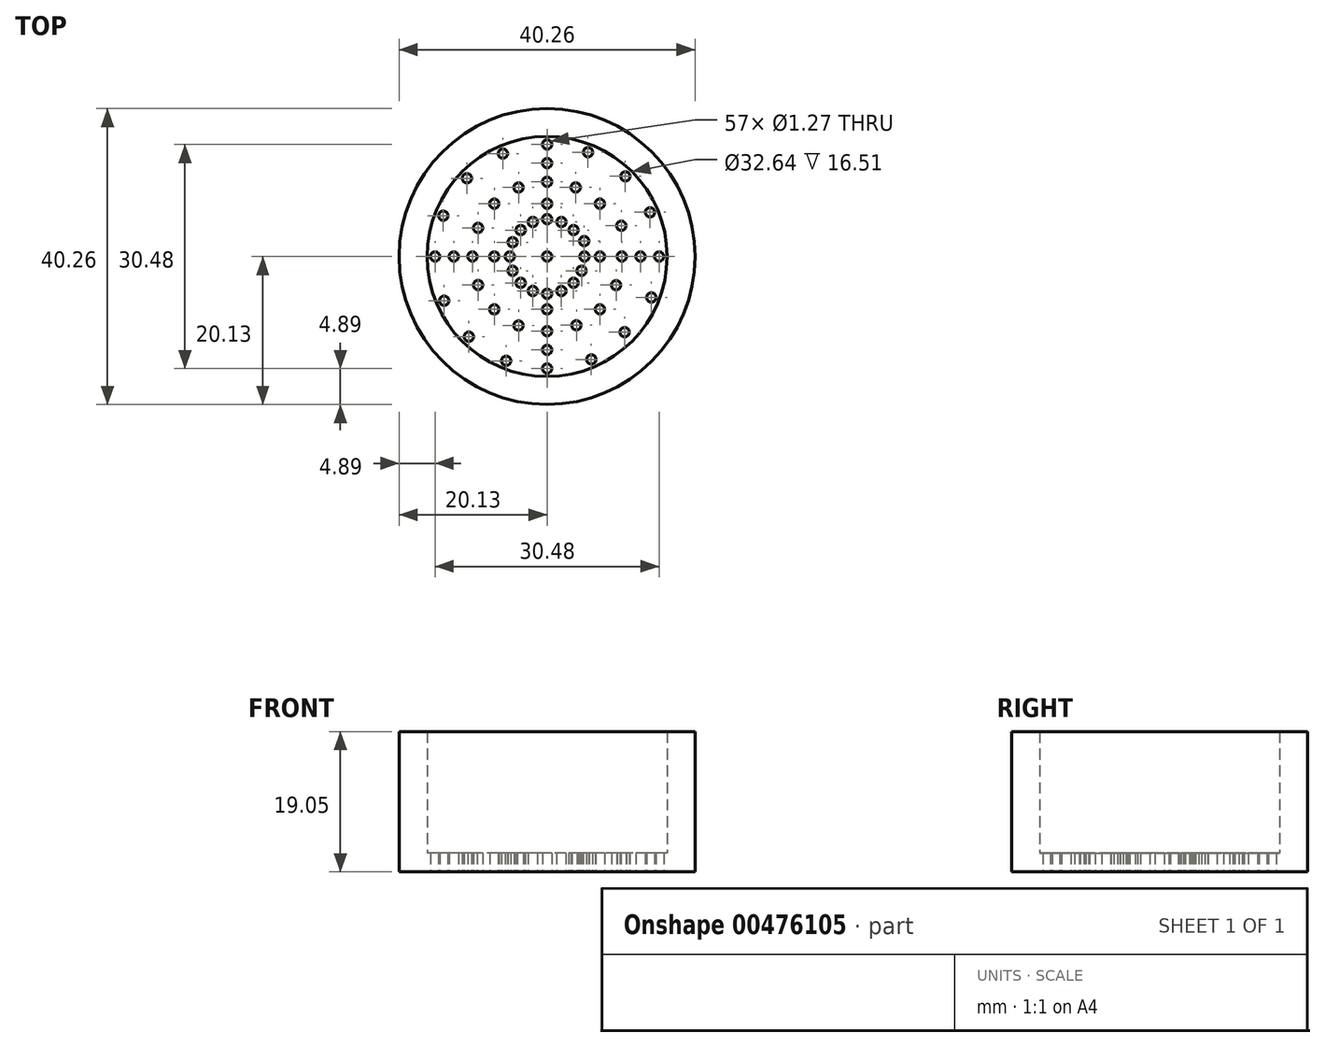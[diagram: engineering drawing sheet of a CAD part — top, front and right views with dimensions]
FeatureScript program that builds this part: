
annotation { "Feature Type Name" : "Feature", "Feature Type Description" : "" }
export const myFeature = defineFeature(function(context is Context, id is Id, definition is map)
    precondition{}
    {
        {
            var Q0;
            Q0=qCreatedBy(makeId("Top.planeOp"),FACE);
            var sketch = newSketch(context, id + "F0", { "sketchPlane" : qUnion([Q0])});
            skCircle(sketch, "E0", {"center": v(0, 0) * mm, "radius": 16.32 * mm});
            skCircle(sketch, "E1", {"center": v(0, 0) * mm, "radius": 20.13 * mm});
            skCircle(sketch, "E2", {"center": v(0, 10.16) * mm, "radius": 0.64 * mm});
            skCircle(sketch, "E3", {"center": v(3.89, 9.39) * mm, "radius": 0.64 * mm});
            skCircle(sketch, "E4", {"center": v(1.94, 4.7) * mm, "radius": 0.64 * mm});
            skCircle(sketch, "E5", {"center": v(3.6, 3.6) * mm, "radius": 0.64 * mm});
            skCircle(sketch, "E6", {"center": v(7.18, 7.18) * mm, "radius": 0.64 * mm});
            skCircle(sketch, "E7", {"center": v(10.1, 4.18) * mm, "radius": 0.64 * mm});
            skCircle(sketch, "E8", {"center": v(10.16, 0) * mm, "radius": 0.64 * mm});
            skCircle(sketch, "E9", {"center": v(-3.89, 9.39) * mm, "radius": 0.64 * mm});
            skCircle(sketch, "E10", {"center": v(-1.94, 4.7) * mm, "radius": 0.64 * mm});
            skCircle(sketch, "E11", {"center": v(5.08, 0) * mm, "radius": 0.64 * mm});
            skCircle(sketch, "E12", {"center": v(9.39, -3.89) * mm, "radius": 0.64 * mm});
            skCircle(sketch, "E13", {"center": v(4.7, -1.94) * mm, "radius": 0.64 * mm});
            skCircle(sketch, "E14", {"center": v(7.18, -7.18) * mm, "radius": 0.64 * mm});
            skCircle(sketch, "E15", {"center": v(3.6, -3.6) * mm, "radius": 0.64 * mm});
            skCircle(sketch, "E16", {"center": v(1.94, -4.7) * mm, "radius": 0.64 * mm});
            skCircle(sketch, "E17", {"center": v(0, -5.08) * mm, "radius": 0.64 * mm});
            skCircle(sketch, "E18", {"center": v(0, -10.16) * mm, "radius": 0.64 * mm});
            skCircle(sketch, "E19", {"center": v(-3.89, -9.39) * mm, "radius": 0.64 * mm});
            skCircle(sketch, "E20", {"center": v(-1.94, -4.7) * mm, "radius": 0.64 * mm});
            skCircle(sketch, "E21", {"center": v(-7.18, -7.18) * mm, "radius": 0.64 * mm});
            skCircle(sketch, "E22", {"center": v(-7.18, 7.18) * mm, "radius": 0.64 * mm});
            skCircle(sketch, "E23", {"center": v(-3.6, 3.6) * mm, "radius": 0.64 * mm});
            skCircle(sketch, "E24", {"center": v(-4.7, 1.94) * mm, "radius": 0.64 * mm});
            skCircle(sketch, "E25", {"center": v(-9.39, 3.89) * mm, "radius": 0.64 * mm});
            skCircle(sketch, "E26", {"center": v(-10.16, 0) * mm, "radius": 0.64 * mm});
            skCircle(sketch, "E27", {"center": v(-5.08, 0) * mm, "radius": 0.64 * mm});
            skCircle(sketch, "E28", {"center": v(-9.39, -3.88) * mm, "radius": 0.64 * mm});
            skCircle(sketch, "E29", {"center": v(0, 7.18) * mm, "radius": 0.64 * mm});
            skCircle(sketch, "E30", {"center": v(7.18, 0) * mm, "radius": 0.64 * mm});
            skCircle(sketch, "E31", {"center": v(0, -7.18) * mm, "radius": 0.64 * mm});
            skCircle(sketch, "E32", {"center": v(-7.18, 0) * mm, "radius": 0.64 * mm});
            skCircle(sketch, "E33", {"center": v(0, 5.08) * mm, "radius": 0.64 * mm});
            skCircle(sketch, "E34", {"center": v(-4.7, -1.94) * mm, "radius": 0.64 * mm});
            skCircle(sketch, "E35", {"center": v(3.98, -9.35) * mm, "radius": 0.64 * mm});
            skCircle(sketch, "E36", {"center": v(0, 0) * mm, "radius": 0.64 * mm});
            skCircle(sketch, "E37", {"center": v(-3.6, -3.6) * mm, "radius": 0.64 * mm});
            skCircle(sketch, "E38", {"center": v(5.05, 2.1) * mm, "radius": 0.64 * mm});
            skCircle(sketch, "E39", {"center": v(0, 15.24) * mm, "radius": 0.64 * mm});
            skCircle(sketch, "E40", {"center": v(5.57, 14.19) * mm, "radius": 0.64 * mm});
            skCircle(sketch, "E41", {"center": v(10.64, 10.9) * mm, "radius": 0.64 * mm});
            skCircle(sketch, "E42", {"center": v(14, 6.01) * mm, "radius": 0.64 * mm});
            skCircle(sketch, "E43", {"center": v(15.24, 0) * mm, "radius": 0.64 * mm});
            skCircle(sketch, "E44", {"center": v(14.19, -5.57) * mm, "radius": 0.64 * mm});
            skCircle(sketch, "E45", {"center": v(6.01, -14) * mm, "radius": 0.64 * mm});
            skCircle(sketch, "E46", {"center": v(0, -15.24) * mm, "radius": 0.64 * mm});
            skCircle(sketch, "E47", {"center": v(-5.57, -14.19) * mm, "radius": 0.64 * mm});
            skCircle(sketch, "E48", {"center": v(-10.64, -10.9) * mm, "radius": 0.64 * mm});
            skCircle(sketch, "E49", {"center": v(-14, -6.01) * mm, "radius": 0.64 * mm});
            skCircle(sketch, "E50", {"center": v(-15.24, 0) * mm, "radius": 0.64 * mm});
            skCircle(sketch, "E51", {"center": v(-14.12, 5.55) * mm, "radius": 0.64 * mm});
            skCircle(sketch, "E52", {"center": v(-10.9, 10.64) * mm, "radius": 0.64 * mm});
            skCircle(sketch, "E53", {"center": v(-6.01, 14) * mm, "radius": 0.64 * mm});
            skCircle(sketch, "E54", {"center": v(10.54, -10.29) * mm, "radius": 0.64 * mm});
            skCircle(sketch, "E55", {"center": v(0, 12.7) * mm, "radius": 0.64 * mm});
            skCircle(sketch, "E56", {"center": v(-12.7, 0) * mm, "radius": 0.64 * mm});
            skCircle(sketch, "E57", {"center": v(0, -12.7) * mm, "radius": 0.64 * mm});
            skCircle(sketch, "E58", {"center": v(12.7, 0) * mm, "radius": 0.64 * mm});
            skSolve(sketch);
        }
        {
            var Q0;
            Q0=makeQuery(id+"F0.imprint","IMPRINT",FACE,{"disambiguationData":[TD([[makeQuery(id+"F0.imprint","IMPRINT",EDGE,{"derivedFrom":sQuery(id+"F0.wireOp",EDGE,"E0")}),1.0]])]});
            extrude(context, id + "F1", {"entities" : qUnion([Q0]), "depth" : 2.54 * mm, "offsetDistance" : 25.4 * mm});
        }
        {
            var Q0;
            Q0=makeQuery(id+"F0.imprint","IMPRINT",FACE,{"disambiguationData":[TD([[makeQuery(id+"F0.imprint","IMPRINT",EDGE,{"derivedFrom":sQuery(id+"F0.wireOp",EDGE,"E0")}),-1.0]])]});
            extrude(context, id + "F2", {"entities" : qUnion([Q0]), "operationType" : NewBodyOperationType.ADD, "depth" : 19.05 * mm, "offsetDistance" : 25.4 * mm});
        }
    });
